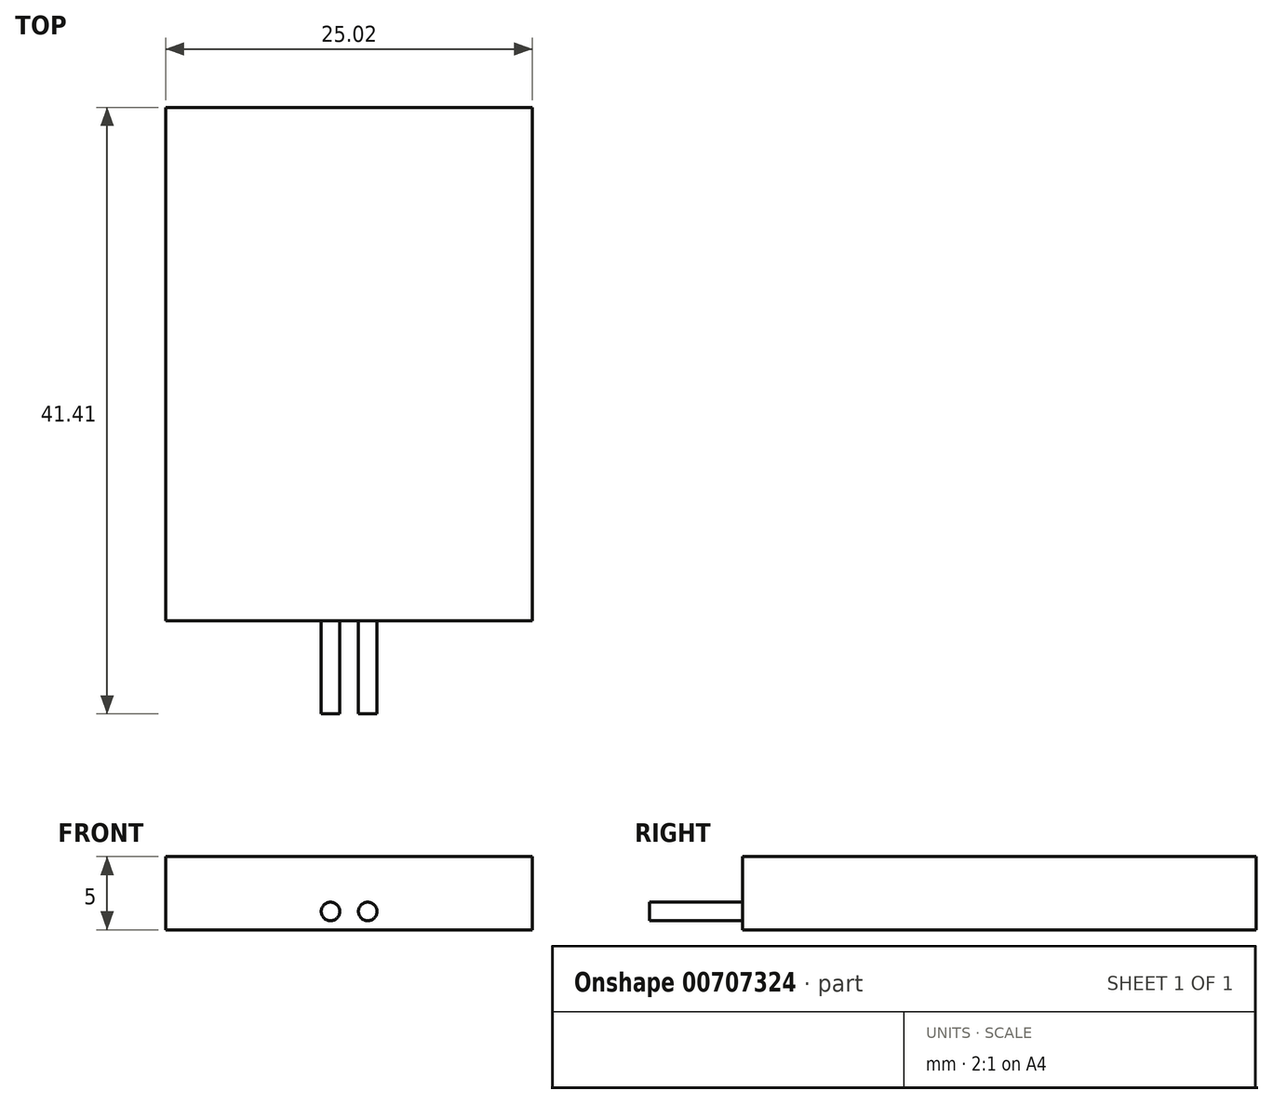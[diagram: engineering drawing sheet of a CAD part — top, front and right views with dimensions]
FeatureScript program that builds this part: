
annotation { "Feature Type Name" : "Feature", "Feature Type Description" : "" }
export const myFeature = defineFeature(function(context is Context, id is Id, definition is map)
    precondition{}
    {
        {
            var Q0;
            Q0=qCreatedBy(makeId("Top.planeOp"),FACE);
            var sketch = newSketch(context, id + "F0", { "sketchPlane" : qUnion([Q0])});
            skLineSegment(sketch, "E0.bottom", {"start": v(-12.5, 17.53) * mm, "end": v(12.5, 17.53) * mm});
            skLineSegment(sketch, "E0.top", {"start": v(-12.5, -17.53) * mm, "end": v(12.5, -17.53) * mm});
            skLineSegment(sketch, "E0.left", {"start": v(-12.5, 17.53) * mm, "end": v(-12.5, -17.53) * mm});
            skLineSegment(sketch, "E0.right", {"start": v(12.5, 17.53) * mm, "end": v(12.5, -17.53) * mm});
            skPoint(sketch, "E1", {"position": v(0, 17.53) * mm});
            skPoint(sketch, "E2", {"position": v(12.5, 0) * mm});
            skSolve(sketch);
        }
        {
            var Q0;
            Q0=makeQuery(id+"F0.imprint","IMPRINT",FACE,{"disambiguationData":[TD([[makeQuery(id+"F0.imprint","IMPRINT",EDGE,{"derivedFrom":sQuery(id+"F0.wireOp",EDGE,"E0.bottom")}),-1.0]])]});
            extrude(context, id + "F1", {"entities" : qUnion([Q0]), "endBound" : BoundingType.SYMMETRIC, "depth" : 5 * mm, "offsetDistance" : 25.4 * mm});
        }
        {
            var Q0;
            Q0=makeQuery(id+"F1.opExtrude","SWEPT_FACE",FACE,{"disambiguationData":[OSD([sQuery(id+"F0.wireOp",EDGE,"E0.top")])]});
            var sketch = newSketch(context, id + "F2", { "sketchPlane" : qUnion([Q0])});
            skCircle(sketch, "E3", {"center": v(-1.27, -1.25) * mm, "radius": 0.64 * mm});
            skLineSegment(sketch, "E4", {"start": v(0, 0) * mm, "end": v(0, -2.5) * mm, "construction": true});
            skPoint(sketch, "E5", {"position": v(0, -1.25) * mm});
            skCircle(sketch, "E6.MirrorC", {"center": v(1.27, -1.25) * mm, "radius": 0.64 * mm});
            skSolve(sketch);
        }
        {
            var Q0;
            Q0 = qSketchRegion(id + "F2", true);
            extrude(context, id + "F3", {"entities" : qUnion([Q0]), "depth" : 6.35 * mm, "offsetDistance" : 25.4 * mm});
        }
    });
